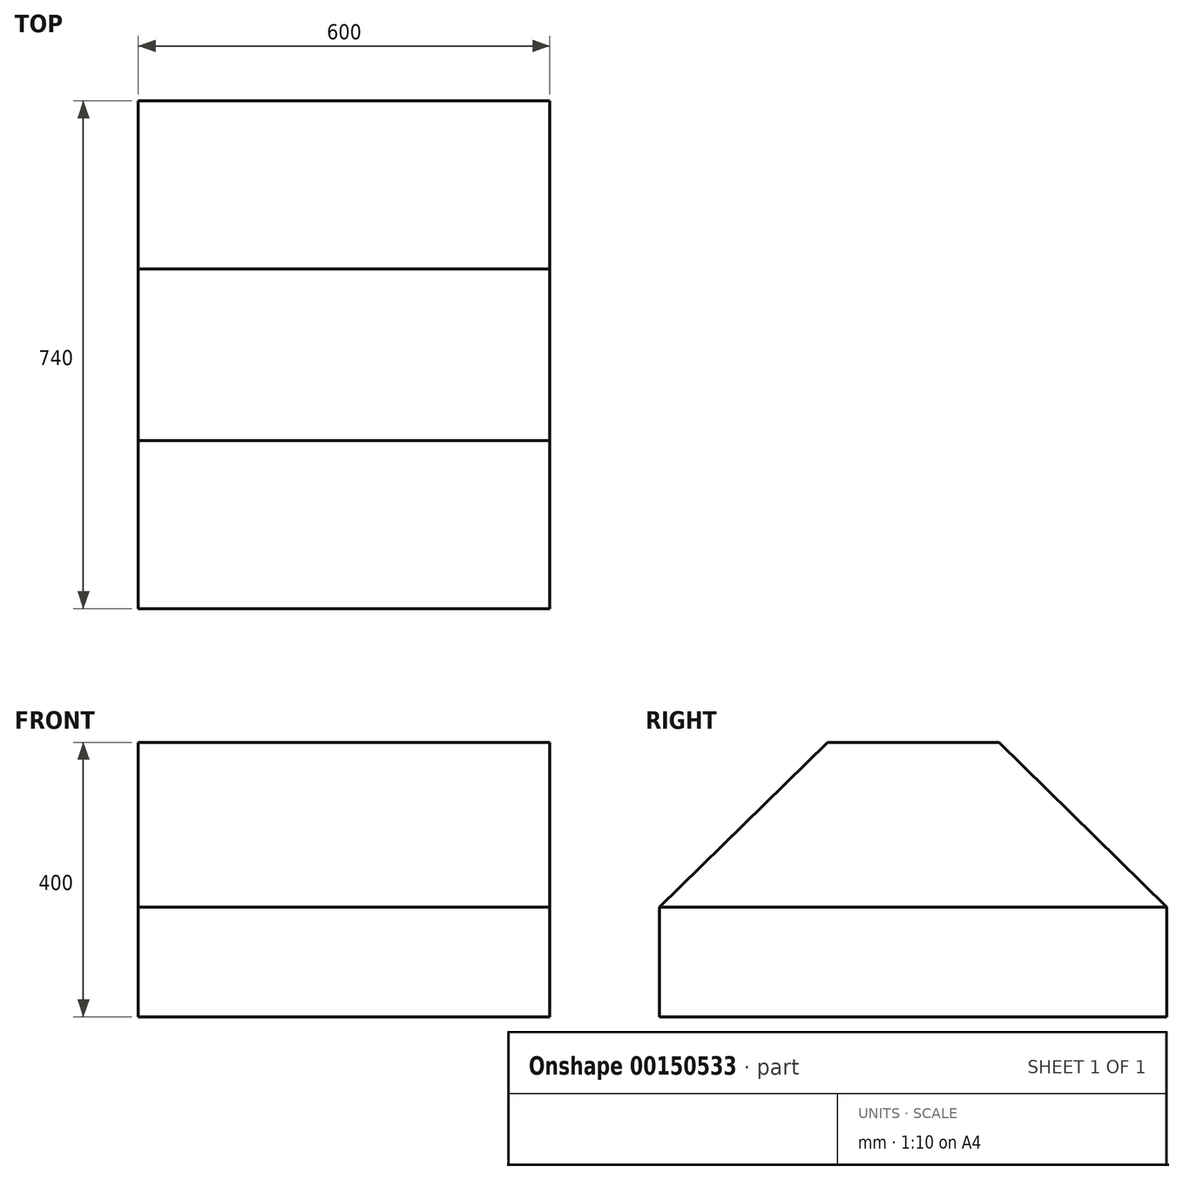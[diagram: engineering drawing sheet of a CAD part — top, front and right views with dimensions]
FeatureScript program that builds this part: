
annotation { "Feature Type Name" : "Feature", "Feature Type Description" : "" }
export const myFeature = defineFeature(function(context is Context, id is Id, definition is map)
    precondition{}
    {
        {
            var Q0;
            Q0=qCreatedBy(makeId("Top.planeOp"),FACE);
            var sketch = newSketch(context, id + "F0", { "sketchPlane" : qUnion([Q0])});
            skLineSegment(sketch, "E0.bottom", {"start": v(272.94, -354.8) * mm, "end": v(-327.06, -354.8) * mm});
            skLineSegment(sketch, "E0.top", {"start": v(272.94, 385.2) * mm, "end": v(-327.06, 385.2) * mm});
            skLineSegment(sketch, "E0.left", {"start": v(272.94, -354.8) * mm, "end": v(272.94, 385.2) * mm});
            skLineSegment(sketch, "E0.right", {"start": v(-327.06, -354.8) * mm, "end": v(-327.06, 385.2) * mm});
            skPoint(sketch, "E0.middle", {"position": v(-27.06, 15.2) * mm});
            skSolve(sketch);
        }
        {
            var Q0;
            Q0 = qSketchRegion(id + "F0", true);
            extrude(context, id + "F1", {"entities" : qUnion([Q0]), "depth" : 160 * mm});
        }
        {
            var Q0;
            Q0=makeQuery(id+"F1.opExtrude","CAP_FACE",FACE,{"disambiguationData":[OSD([sQuery(id+"F0.wireOp",EDGE,"E0.bottom"),sQuery(id+"F0.wireOp",EDGE,"E0.top"),sQuery(id+"F0.wireOp",EDGE,"E0.left"),sQuery(id+"F0.wireOp",EDGE,"E0.right")])],"isStart":false});
            var sketch = newSketch(context, id + "F2", { "sketchPlane" : qUnion([Q0])});
            skLineSegment(sketch, "E1.bottom", {"start": v(-327.06, 385.2) * mm, "end": v(272.94, 385.2) * mm});
            skLineSegment(sketch, "E1.top", {"start": v(-327.06, -354.8) * mm, "end": v(272.94, -354.8) * mm});
            skLineSegment(sketch, "E1.left", {"start": v(-327.06, 385.2) * mm, "end": v(-327.06, -354.8) * mm});
            skLineSegment(sketch, "E1.right", {"start": v(272.94, 385.2) * mm, "end": v(272.94, -354.8) * mm});
            skSolve(sketch);
        }
        {
            var Q0;
            Q0 = qSketchRegion(id + "F2", true);
            extrude(context, id + "F3", {"entities" : qUnion([Q0]), "depth" : 240 * mm});
        }
        {
            var Q0;
            Q0=makeQuery(id+"F3.opExtrude","SWEPT_FACE",FACE,{"disambiguationData":[OSD([sQuery(id+"F2.wireOp",EDGE,"E1.right")])]});
            var sketch = newSketch(context, id + "F4", { "sketchPlane" : qUnion([Q0])});
            skLineSegment(sketch, "E2", {"start": v(-109.8, 400) * mm, "end": v(-354.8, 160) * mm});
            skLineSegment(sketch, "E3", {"start": v(140.2, 400) * mm, "end": v(385.2, 160) * mm});
            skSolve(sketch);
        }
        {
            var Q0;
            Q0 = qSketchRegion(id + "F4", true);
            var Q1;
            {var subQ0=sQuery(id+"F4.wireOp",EDGE,"E2");Q1=makeQuery(id+"F4.imprint","IMPRINT",FACE,{"disambiguationData":[TD([[makeQuery(id+"F4.imprint","IMPRINT",EDGE,{"derivedFrom":subQ0}),-1.0]])]});}
            var Q2;
            {var subQ0=sQuery(id+"F4.wireOp",EDGE,"E3");Q2=makeQuery(id+"F4.imprint","IMPRINT",FACE,{"disambiguationData":[TD([[makeQuery(id+"F4.imprint","IMPRINT",EDGE,{"derivedFrom":subQ0}),1.0]])]});}
            extrude(context, id + "F5", {"entities" : qUnion([Q0, Q1, Q2]), "operationType" : NewBodyOperationType.REMOVE, "endBound" : BoundingType.THROUGH_ALL, "oppositeDirection" : true, "depth" : 25 * mm});
        }
    });
